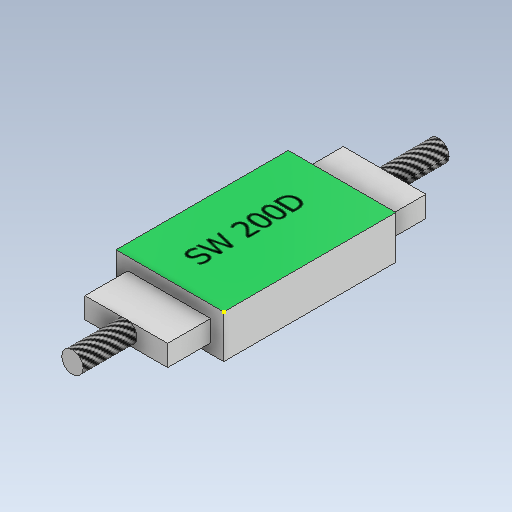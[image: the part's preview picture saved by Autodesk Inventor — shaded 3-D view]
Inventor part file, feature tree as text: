
AUTODESK INVENTOR PART (.ipt)
format: ipt  version: 2021 (Build 250183000, 183)  size: 140,800 bytes
history: native  units: mm
features: sketch x6, extrude x5
ambient origin geometry x8: Origin, YZ Plane, XZ Plane, XY Plane, X Axis, Y Axis, Z Axis, Center Point
bodies: Solid1 (feature_tree)
feature tree (11):
  extrude  "Extrusion1"  Depth=50.0mm
  extrude  "Extrusion2"  Depth=20.0mm TaperAngle=0.0deg
  extrude  "Extrusion3"  Depth=25.0mm TaperAngle=0.0deg
  extrude  "Extrusion4"  [1 undecoded]
  extrude  "Extrusion5"  [1 undecoded]
  sketch  "Sketch6"
  sketch  "Sketch1"  dims[d0=80.0mm d1=50.0mm]
  sketch  "Sketch2"  dims[d2=20.0mm d3=0.0mm d4=20.0mm d5=0.0mm]
  sketch  "Sketch3"  dims[d6=20.0mm d7=0.0mm d8=25.0mm d9=0.0mm]
  sketch  "Sketch4"  dims[d10=25.0mm d11=0.0mm]
  sketch  "Sketch5"
note: 2 required parameter values undecoded (feature->parameter linkage not recoverable at this tier; creation-order binding heuristic only, values carry confidence <= 0.55)
